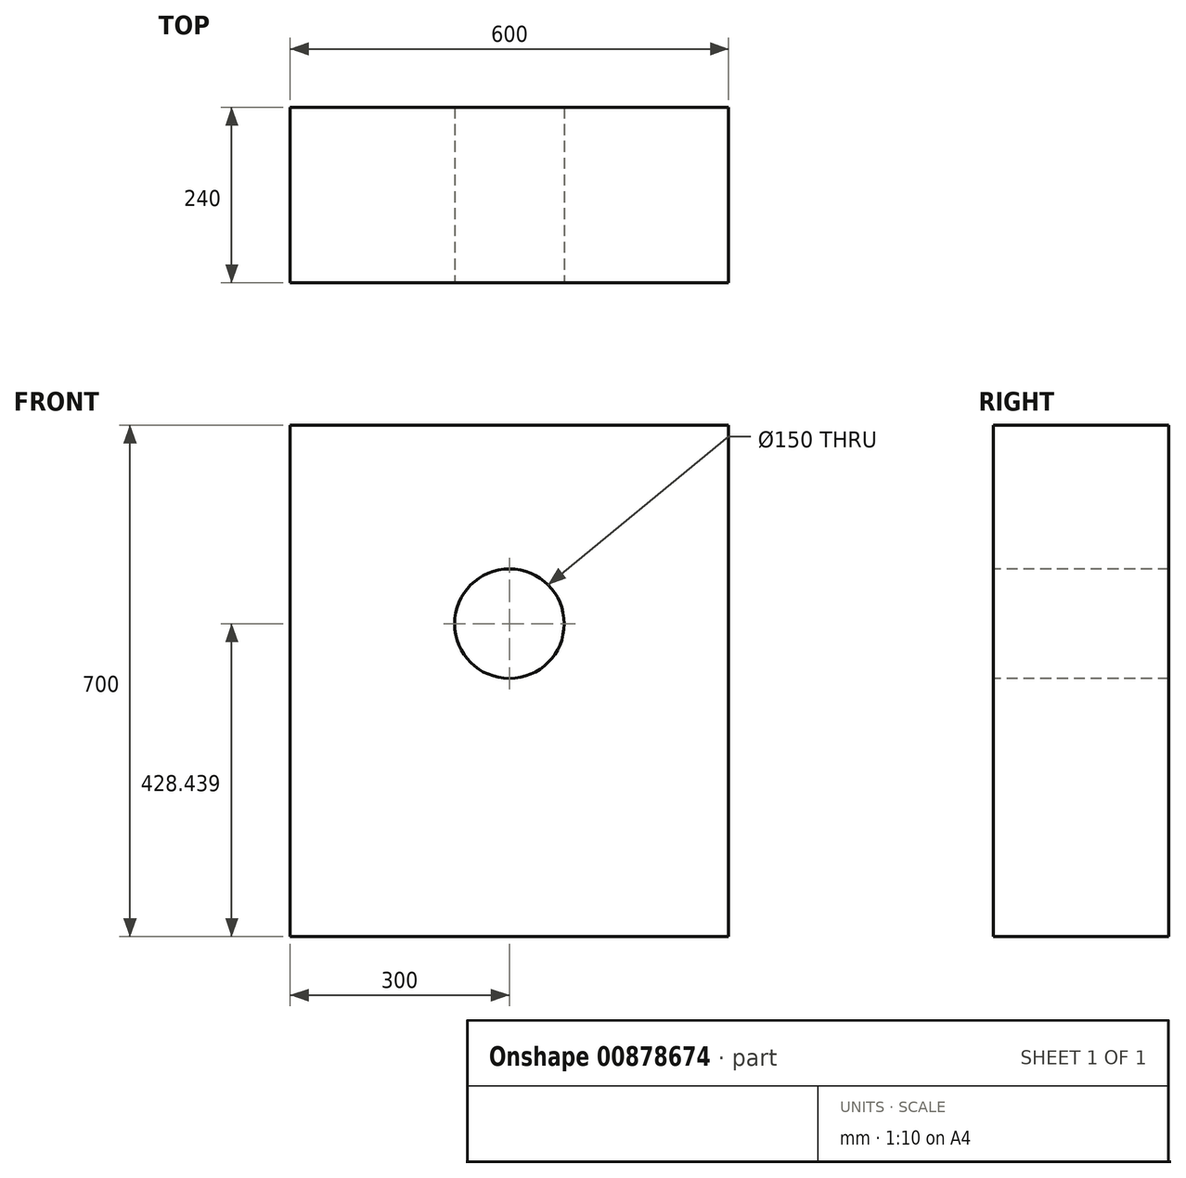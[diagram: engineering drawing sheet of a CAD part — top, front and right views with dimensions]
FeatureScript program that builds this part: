
annotation { "Feature Type Name" : "Feature", "Feature Type Description" : "" }
export const myFeature = defineFeature(function(context is Context, id is Id, definition is map)
    precondition{}
    {
        {
            var Q0;
            Q0=qCreatedBy(makeId("Front.planeOp"),FACE);
            var sketch = newSketch(context, id + "F0", { "sketchPlane" : qUnion([Q0])});
            skLineSegment(sketch, "E0.bottom", {"start": v(-300, 350) * mm, "end": v(300, 350) * mm});
            skLineSegment(sketch, "E0.top", {"start": v(-300, -350) * mm, "end": v(300, -350) * mm});
            skLineSegment(sketch, "E0.left", {"start": v(-300, 350) * mm, "end": v(-300, -350) * mm});
            skLineSegment(sketch, "E0.right", {"start": v(300, 350) * mm, "end": v(300, -350) * mm});
            skPoint(sketch, "E0.middle", {"position": v(0, 0) * mm});
            skSolve(sketch);
        }
        {
            var Q0;
            Q0=makeQuery(id+"F0.imprint","IMPRINT",FACE,{"disambiguationData":[TD([[makeQuery(id+"F0.imprint","IMPRINT",EDGE,{"derivedFrom":sQuery(id+"F0.wireOp",EDGE,"E0.bottom")}),-1.0]])]});
            extrude(context, id + "F1", {"entities" : qUnion([Q0]), "depth" : 240 * mm, "offsetDistance" : 25 * mm});
        }
        {
            var Q0;
            Q0=makeQuery(id+"F1.opExtrude","CAP_FACE",FACE,{"disambiguationData":[OSD([sQuery(id+"F0.wireOp",EDGE,"E0.bottom"),sQuery(id+"F0.wireOp",EDGE,"E0.top"),sQuery(id+"F0.wireOp",EDGE,"E0.left"),sQuery(id+"F0.wireOp",EDGE,"E0.right")])],"isStart":false});
            var sketch = newSketch(context, id + "F2", { "sketchPlane" : qUnion([Q0])});
            skLineSegment(sketch, "E1", {"start": v(0, 350) * mm, "end": v(0, 96.73) * mm});
            skSolve(sketch);
        }
        {
            var Q0;
            Q0=makeQuery(id+"F2.imprint","IMPRINT",FACE,{"disambiguationData":[TD([[makeQuery(id+"F2.imprint","IMPRINT",EDGE,{"derivedFrom":makeQuery(id+"F1.opExtrude","CAP_EDGE",EDGE,{"disambiguationData":[OSD([sQuery(id+"F0.wireOp",EDGE,"E0.top")])],"isStart":false})}),1.0]])]});
            var sketch = newSketch(context, id + "F3", { "sketchPlane" : qUnion([Q0])});
            skCircle(sketch, "E2", {"center": v(0, 78.44) * mm, "radius": 75 * mm});
            skArc(sketch, "E3", {"start": v(-150, 78.44) * mm, "mid": v(0, -71.56) * mm, "end": v(150, 78.44) * mm});
            skLineSegment(sketch, "E4.left", {"start": v(150, 349.84) * mm, "end": v(150, 78.44) * mm});
            skLineSegment(sketch, "E4.right", {"start": v(-150, 351.4) * mm, "end": v(-150, 78.44) * mm});
            skPoint(sketch, "E5.orphan", {"position": v(150, -243.26) * mm});
            skPoint(sketch, "E6.orphan", {"position": v(-150, -243.26) * mm});
            skPoint(sketch, "E7.orphan", {"position": v(-150, 400.14) * mm});
            skPoint(sketch, "E8.orphan", {"position": v(150, 400.14) * mm});
            skSolve(sketch);
        }
        {
            var Q0;
            Q0=makeQuery(id+"F3.imprint","IMPRINT",FACE,{"disambiguationData":[TD([[makeQuery(id+"F3.imprint","IMPRINT",EDGE,{"derivedFrom":sQuery(id+"F3.wireOp",EDGE,"E2")}),1.0]])]});
            extrude(context, id + "F4", {"entities" : qUnion([Q0]), "operationType" : NewBodyOperationType.REMOVE, "endBound" : BoundingType.THROUGH_ALL, "oppositeDirection" : true, "depth" : 25 * mm, "offsetDistance" : 25 * mm});
        }
    });
